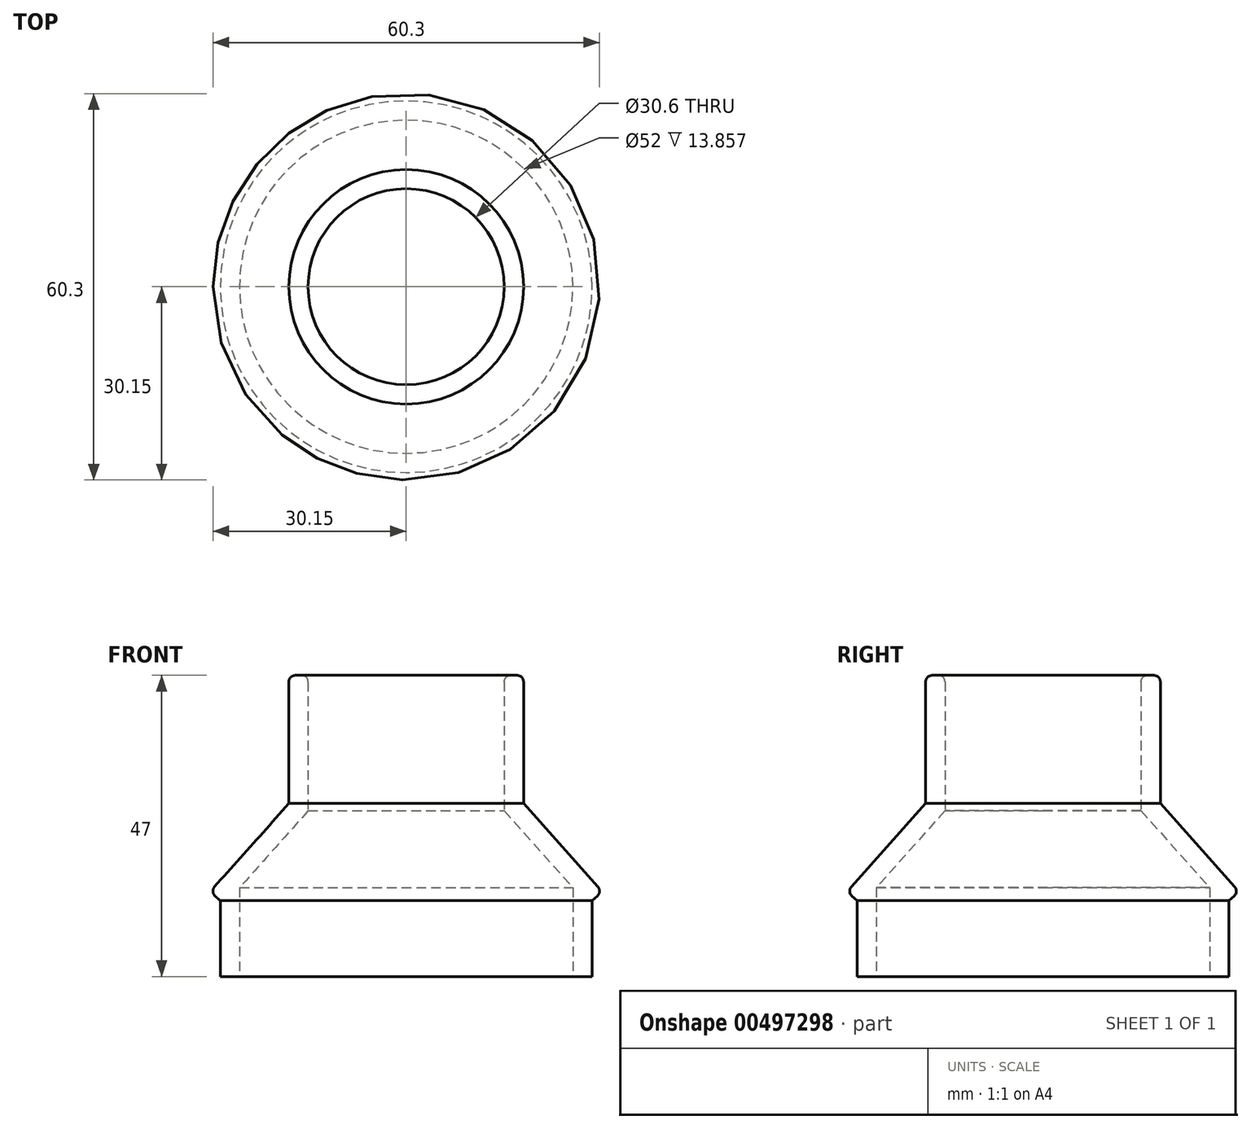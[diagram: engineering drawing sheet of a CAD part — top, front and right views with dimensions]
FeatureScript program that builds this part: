
annotation { "Feature Type Name" : "Feature", "Feature Type Description" : "" }
export const myFeature = defineFeature(function(context is Context, id is Id, definition is map)
    precondition{}
    {
        {
            var Q0;
            Q0=qCreatedBy(makeId("Right.planeOp"),FACE);
            var sketch = newSketch(context, id + "F0", { "sketchPlane" : qUnion([Q0])});
            skLineSegment(sketch, "E0", {"start": v(29, 0) * mm, "end": v(29, 11.85) * mm});
            skLineSegment(sketch, "E1", {"start": v(29, 15) * mm, "end": v(18.3, 27) * mm});
            skLineSegment(sketch, "E2", {"start": v(18.3, 27) * mm, "end": v(18.3, 47) * mm});
            skLineSegment(sketch, "E3.0", {"start": v(15.3, 25.86) * mm, "end": v(15.3, 47) * mm});
            skLineSegment(sketch, "E3.1", {"start": v(26, 13.86) * mm, "end": v(15.3, 25.86) * mm});
            skLineSegment(sketch, "E3.2", {"start": v(26, 0) * mm, "end": v(26, 13.86) * mm});
            skLineSegment(sketch, "E4", {"start": v(15.3, 47) * mm, "end": v(18.3, 47) * mm});
            skLineSegment(sketch, "E5", {"start": v(29, 0) * mm, "end": v(26, 0) * mm});
            skLineSegment(sketch, "E6", {"start": v(0, 0) * mm, "end": v(0, 47) * mm, "construction": true});
            skLineSegment(sketch, "E7", {"start": v(29, 15) * mm, "end": v(30.57, 13.24) * mm});
            skLineSegment(sketch, "E8", {"start": v(30.57, 13.24) * mm, "end": v(29, 11.85) * mm});
            skSolve(sketch);
        }
        {
            var Q0;
            Q0 = qSketchRegion(id + "F0", true);
            var Q1;
            Q1=sQuery(id+"F0.wireOp",EDGE,"E6");
            revolve(context, id + "F1", {"entities" : qUnion([Q0]), "axis" : qUnion([Q1]), "revolveType" : RevolveType.FULL});
        }
        {
            var Q0;
            Q0=makeQuery(id+"F1.opRevolve","SWEPT_FACE",FACE,{"disambiguationData":[OSD([sQuery(id+"F0.wireOp",EDGE,"E4")])]});
            var Q1;
            Q1=makeQuery(id+"F1.opRevolve","SWEPT_EDGE",EDGE,{"disambiguationData":[OSD([sQuery(id+"F0.wireOp",EDGE,"E7"),sQuery(id+"F0.wireOp",EDGE,"E8")])]});
            fillet(context, id + "F2", {"entities" : qUnion([Q0, Q1]), "radius" : 1 * mm, "tangentPropagation" : true, "allowEdgeOverflow" : false});
        }
    });
